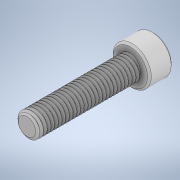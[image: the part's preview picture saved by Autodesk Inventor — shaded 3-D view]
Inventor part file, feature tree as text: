
AUTODESK INVENTOR PART (.ipt)
format: ipt  version: 2021 (Build 250183000, 183)  size: 883,712 bytes
history: native  units: in
note: dims shown in document units (in); Inventor stores cm internally (conversion verified against a paired STEP export)
features: chamfer x1
ambient origin geometry x8: Origin, YZ Plane, XZ Plane, XY Plane, X Axis, Y Axis, Z Axis, Center Point
bodies: Solid1 (feature_tree)
feature tree (1):
  chamfer  "Chamfer1"  [1 undecoded]
note: 1 required parameter value undecoded (feature->parameter linkage not recoverable at this tier; creation-order binding heuristic only, values carry confidence <= 0.55)
